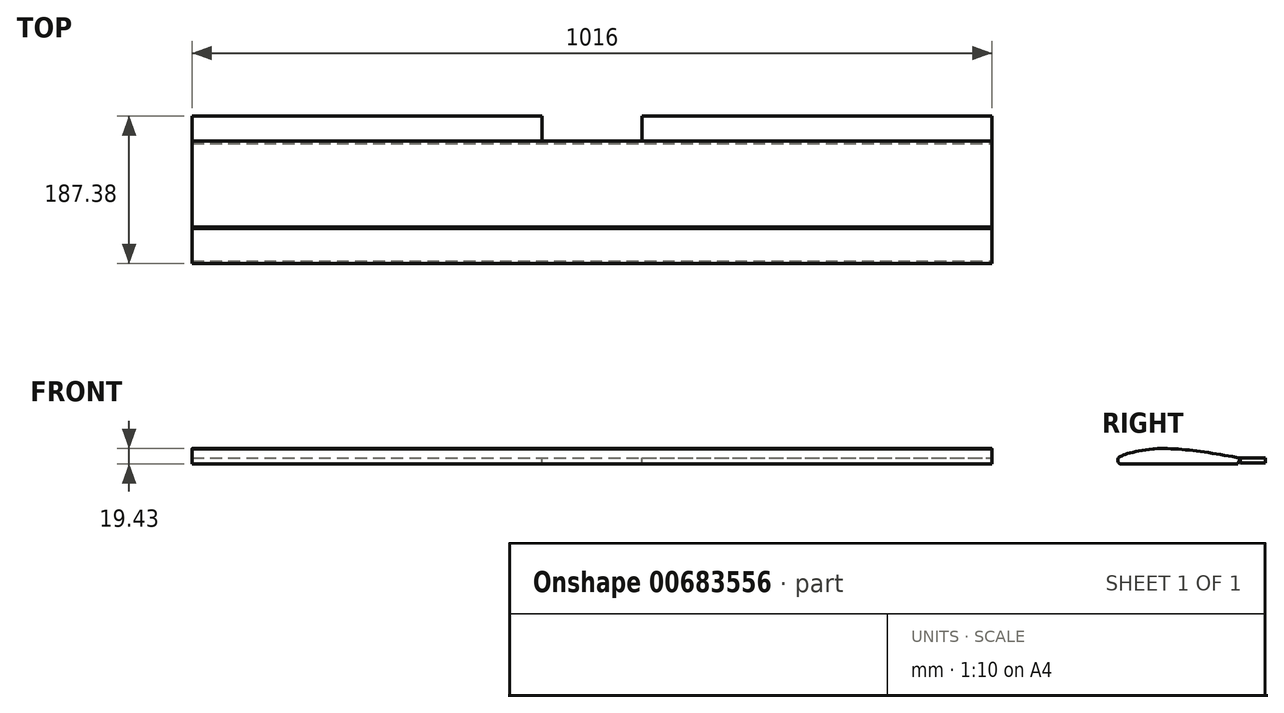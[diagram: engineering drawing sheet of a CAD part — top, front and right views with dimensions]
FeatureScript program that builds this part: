
annotation { "Feature Type Name" : "Feature", "Feature Type Description" : "" }
export const myFeature = defineFeature(function(context is Context, id is Id, definition is map)
    precondition{}
    {
        {
            var Q0;
            Q0=qCreatedBy(makeId("Right.planeOp"),FACE);
            var sketch = newSketch(context, id + "F0", { "sketchPlane" : qUnion([Q0])});
            skCircle(sketch, "E0", {"center": v(-42.99, 9.52) * mm, "radius": 9.52 * mm});
            skFitSpline(sketch, "E1", {"points": [v(-86, -0.01) * mm, v(-88.76, 2.6) * mm, v(-89, 6.62) * mm, v(-86, 9.44) * mm, v(-44.49, 18.93) * mm, v(66.4, 7.32) * mm], "startDerivative": vector(-43.28, 24.23) * mm, "endDerivative": vector(263.54, -46.57) * mm});
            skLineSegment(sketch, "E2", {"start": v(66.4, 7.32) * mm, "end": v(63.54, -0.01) * mm});
            skLineSegment(sketch, "E3", {"start": v(63.54, -0.01) * mm, "end": v(-86, -0.01) * mm});
            skLineSegment(sketch, "E4", {"start": v(66.4, 7.32) * mm, "end": v(66.4, 0.98) * mm});
            skLineSegment(sketch, "E5", {"start": v(66.4, 0.98) * mm, "end": v(98.15, 0.98) * mm});
            skLineSegment(sketch, "E6", {"start": v(66.4, 7.32) * mm, "end": v(98.15, 7.32) * mm});
            skLineSegment(sketch, "E7", {"start": v(98.15, 7.32) * mm, "end": v(98.15, 0.98) * mm});
            skSolve(sketch);
        }
        {
            var Q0;
            Q0 = qSketchRegion(id + "F0", true);
            extrude(context, id + "F1", {"entities" : qUnion([Q0]), "endBound" : BoundingType.SYMMETRIC, "oppositeDirection" : true, "depth" : 1016 * mm, "offsetDistance" : 25.4 * mm});
        }
        {
            var Q0;
            Q0=makeQuery(id+"F1.opExtrude","SWEPT_FACE",FACE,{"disambiguationData":[OSD([sQuery(id+"F0.wireOp",EDGE,"E6")])]});
            var sketch = newSketch(context, id + "F2", { "sketchPlane" : qUnion([Q0])});
            skLineSegment(sketch, "E8.bottom", {"start": v(0, 98.15) * mm, "end": v(-63.5, 98.15) * mm});
            skLineSegment(sketch, "E8.top", {"start": v(0, 66.4) * mm, "end": v(-63.5, 66.4) * mm});
            skLineSegment(sketch, "E8.left", {"start": v(0, 98.15) * mm, "end": v(0, 66.4) * mm});
            skLineSegment(sketch, "E8.right", {"start": v(-63.5, 98.15) * mm, "end": v(-63.5, 66.4) * mm});
            skLineSegment(sketch, "E9.bottom", {"start": v(0, 98.15) * mm, "end": v(63.5, 98.15) * mm});
            skLineSegment(sketch, "E9.top", {"start": v(0, 66.4) * mm, "end": v(63.5, 66.4) * mm});
            skLineSegment(sketch, "E9.right", {"start": v(63.5, 98.15) * mm, "end": v(63.5, 66.4) * mm});
            skSolve(sketch);
        }
        {
            var Q0;
            Q0 = qSketchRegion(id + "F2", true);
            extrude(context, id + "F3", {"entities" : qUnion([Q0]), "operationType" : NewBodyOperationType.REMOVE, "oppositeDirection" : true, "depth" : 25.4 * mm, "offsetDistance" : 25.4 * mm});
        }
    });
